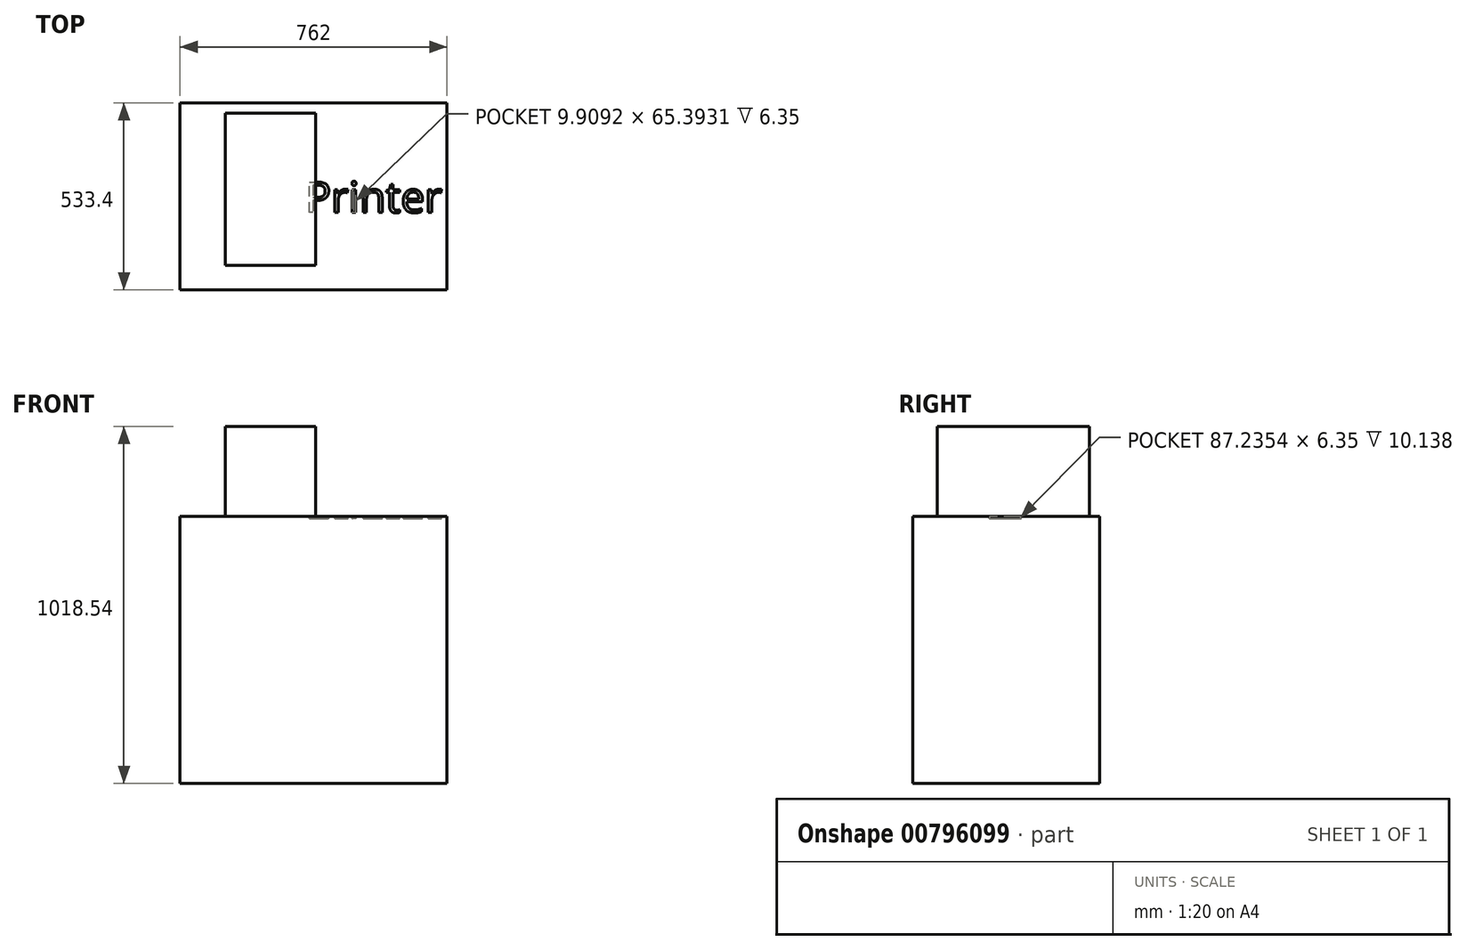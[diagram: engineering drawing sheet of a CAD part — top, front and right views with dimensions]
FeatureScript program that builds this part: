
annotation { "Feature Type Name" : "Feature", "Feature Type Description" : "" }
export const myFeature = defineFeature(function(context is Context, id is Id, definition is map)
    precondition{}
    {
        {
            var Q0;
            Q0=qCreatedBy(makeId("Top.planeOp"),FACE);
            var sketch = newSketch(context, id + "F0", { "sketchPlane" : qUnion([Q0])});
            skLineSegment(sketch, "E0.bottom", {"start": v(0, 0) * mm, "end": v(762, 0) * mm});
            skLineSegment(sketch, "E0.top", {"start": v(0, 533.4) * mm, "end": v(762, 533.4) * mm});
            skLineSegment(sketch, "E0.left", {"start": v(0, 0) * mm, "end": v(0, 533.4) * mm});
            skLineSegment(sketch, "E0.right", {"start": v(762, 0) * mm, "end": v(762, 533.4) * mm});
            skSolve(sketch);
        }
        {
            var Q0;
            Q0 = qSketchRegion(id + "F0", true);
            extrude(context, id + "F1", {"entities" : qUnion([Q0]), "depth" : 762 * mm, "offsetDistance" : 25.4 * mm});
        }
        {
            var Q0;
            Q0=makeQuery(id+"F1.opExtrude","CAP_FACE",FACE,{"disambiguationData":[OSD([sQuery(id+"F0.wireOp",EDGE,"E0.bottom"),sQuery(id+"F0.wireOp",EDGE,"E0.top"),sQuery(id+"F0.wireOp",EDGE,"E0.left"),sQuery(id+"F0.wireOp",EDGE,"E0.right")])],"isStart":false});
            var sketch = newSketch(context, id + "F2", { "sketchPlane" : qUnion([Q0])});
            skLineSegment(sketch, "E1.bottom", {"start": v(129.6, 70.23) * mm, "end": v(386.54, 70.23) * mm});
            skLineSegment(sketch, "E1.top", {"start": v(129.6, 504.72) * mm, "end": v(386.54, 504.72) * mm});
            skLineSegment(sketch, "E1.left", {"start": v(129.6, 70.23) * mm, "end": v(129.6, 504.72) * mm});
            skLineSegment(sketch, "E1.right", {"start": v(386.54, 70.23) * mm, "end": v(386.54, 504.72) * mm});
            skSolve(sketch);
        }
        {
            var Q0;
            Q0 = qSketchRegion(id + "F2", true);
            extrude(context, id + "F3", {"entities" : qUnion([Q0]), "operationType" : NewBodyOperationType.ADD, "depth" : 256.54 * mm, "offsetDistance" : 25.4 * mm});
        }
        {
            var Q0;
            Q0=makeQuery(id+"F1.opExtrude","CAP_FACE",FACE,{"disambiguationData":[OSD([sQuery(id+"F0.wireOp",EDGE,"E0.bottom"),sQuery(id+"F0.wireOp",EDGE,"E0.top"),sQuery(id+"F0.wireOp",EDGE,"E0.left"),sQuery(id+"F0.wireOp",EDGE,"E0.right")])],"isStart":false});
            var sketch = newSketch(context, id + "F4", { "sketchPlane" : qUnion([Q0])});
            skText(sketch, "E2", { "text": "Printer", "fontName": "OpenSans-Regular.ttf"});
            const initialGuessF4  = {"E2": [0.35726, 0.2205, 1, 0, 0.08798]};
            skSetInitialGuess(sketch, initialGuessF4);
            skSolve(sketch);
        }
        {
            var Q0;
            Q0 = qSketchRegion(id + "F4", true);
            extrude(context, id + "F5", {"entities" : qUnion([Q0]), "operationType" : NewBodyOperationType.REMOVE, "oppositeDirection" : true, "depth" : 6.35 * mm, "offsetDistance" : 25.4 * mm});
        }
        {
            var Q0;
            Q0 = qSketchRegion(id + "F4", true);
            extrude(context, id + "F6", {"entities" : qUnion([Q0]), "operationType" : NewBodyOperationType.REMOVE, "oppositeDirection" : true, "depth" : 6.35 * mm, "offsetDistance" : 25.4 * mm});
        }
    });
